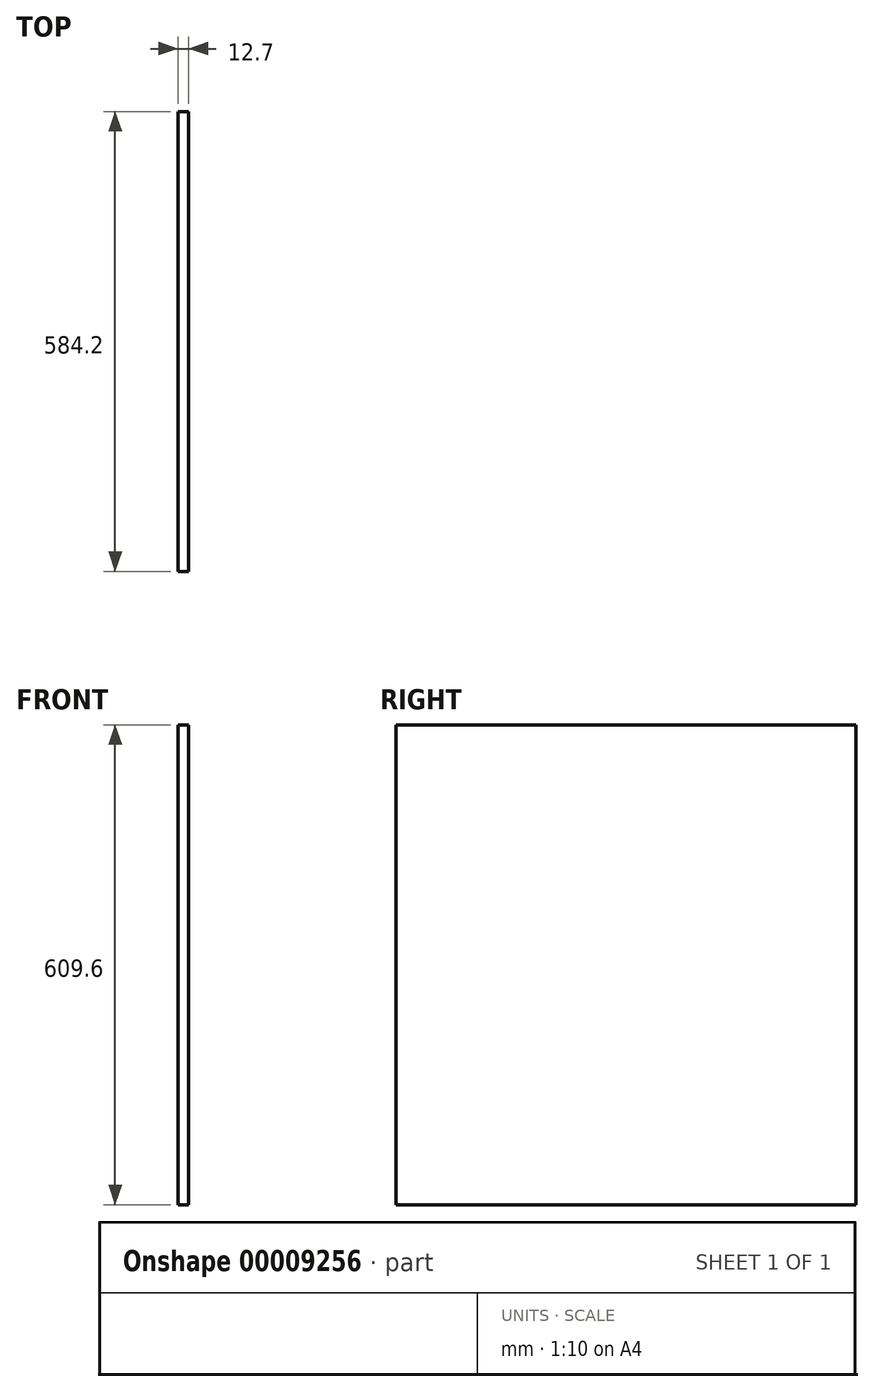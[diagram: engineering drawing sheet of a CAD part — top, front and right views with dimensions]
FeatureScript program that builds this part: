
annotation { "Feature Type Name" : "Feature", "Feature Type Description" : "" }
export const myFeature = defineFeature(function(context is Context, id is Id, definition is map)
    precondition{}
    {
        {
            var Q0;
            Q0=qCreatedBy(makeId("Right.planeOp"),FACE);
            var sketch = newSketch(context, id + "F0", { "sketchPlane" : qUnion([Q0])});
            skLineSegment(sketch, "E0.rect.bottom", {"start": v(292.1, 304.8) * mm, "end": v(-292.1, 304.8) * mm});
            skLineSegment(sketch, "E0.rect.top", {"start": v(292.1, -304.8) * mm, "end": v(-292.1, -304.8) * mm});
            skLineSegment(sketch, "E0.rect.left", {"start": v(292.1, 304.8) * mm, "end": v(292.1, -304.8) * mm});
            skLineSegment(sketch, "E0.rect.right", {"start": v(-292.1, 304.8) * mm, "end": v(-292.1, -304.8) * mm});
            skPoint(sketch, "E0.rect.middle", {"position": v(0, 0) * mm});
            skSolve(sketch);
        }
        {
            var Q0;
            Q0=makeQuery(id+"F0.imprint","IMPRINT",FACE,{"disambiguationData":[TD([[makeQuery(id+"F0.imprint","IMPRINT",EDGE,{"derivedFrom":sQuery(id+"F0.wireOp",EDGE,"E0.rect.bottom")}),1.0]])]});
            extrude(context, id + "F1", {"entities" : qUnion([Q0]), "depth" : 12.7 * mm});
        }
    });
